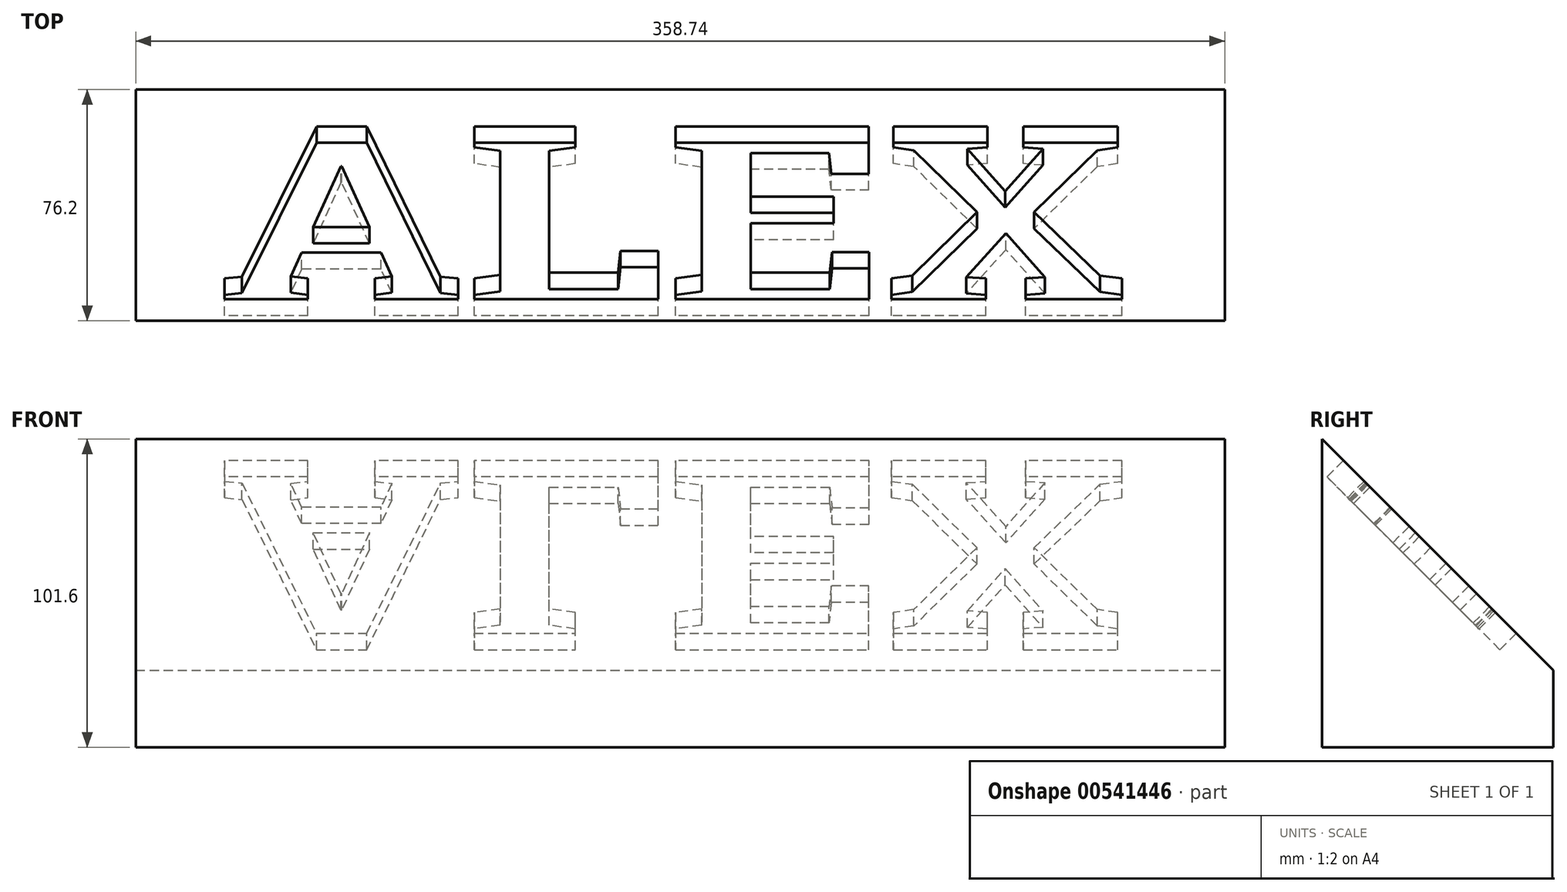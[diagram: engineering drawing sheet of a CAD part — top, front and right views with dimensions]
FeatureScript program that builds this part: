
annotation { "Feature Type Name" : "Feature", "Feature Type Description" : "" }
export const myFeature = defineFeature(function(context is Context, id is Id, definition is map)
    precondition{}
    {
        {
            var Q0;
            Q0=qCreatedBy(makeId("Top.planeOp"),FACE);
            var sketch = newSketch(context, id + "F0", { "sketchPlane" : qUnion([Q0])});
            skLineSegment(sketch, "E0.left", {"start": v(179.37, -152.4) * mm, "end": v(179.37, -76.2) * mm});
            skLineSegment(sketch, "E0.right", {"start": v(-179.37, -152.4) * mm, "end": v(-179.37, -76.2) * mm});
            skLineSegment(sketch, "E1", {"start": v(-179.37, -76.2) * mm, "end": v(179.37, -76.2) * mm});
            skLineSegment(sketch, "E2", {"start": v(-179.37, -152.4) * mm, "end": v(179.37, -152.4) * mm});
            skSolve(sketch);
        }
        {
            var Q0;
            {var subQ0=sQuery(id+"F0.wireOp",EDGE,"E0.left");Q0=makeQuery(id+"F0.imprint","IMPRINT",FACE,{"disambiguationData":[TD([[makeQuery(id+"F0.imprint","IMPRINT",EDGE,{"derivedFrom":subQ0}),1.0]])]});}
            var Q1;
            {var subQ0=sQuery(id+"F0.wireOp",EDGE,"f78de060-f92b-4e90-a891-c1896b122fa7.2");var subQ1=sQuery(id+"F0.wireOp",EDGE,"f78de060-f92b-4e90-a891-c1896b122fa7.1");var subQ2=makeQuery(id+"F0.imprint","INTERSECT",VERTEX,{"derivedFrom":[subQ1,subQ0]});Q1=makeQuery(id+"F0.imprint","IMPRINT",FACE,{"disambiguationData":[TD([[makeQuery(id+"F0.imprint","IMPRINT",EDGE,{"disambiguationData":[TD([[subQ2,1.0]])],"derivedFrom":subQ1}),-1.0]])]});}
            extrude(context, id + "F1", {"entities" : qUnion([Q0, Q1]), "depth" : 101.6 * mm, "offsetDistance" : 25.4 * mm});
        }
        {
            var Q0;
            Q0=makeQuery(id+"F1.opExtrude","CAP_EDGE",EDGE,{"disambiguationData":[OSD([sQuery(id+"F0.wireOp",EDGE,"E1")])],"isStart":false});
            chamfer(context, id + "F2", {"entities" : qUnion([Q0]), "width" : 76.2 * mm, "tangentPropagation" : true});
        }
        {
            var Q0;
            Q0=makeQuery(id+"F2.opChamfer","BLEND_FACE",FACE,{"disambiguationData":[OSD([sQuery(id+"F0.wireOp",EDGE,"E1")])]});
            cPlane(context, id + "F3", {"entities" : qUnion([Q0]), "cplaneType" : CPlaneType.OFFSET, "offset" : 0 * mm, "width" : 152.4 * mm, "height" : 152.4 * mm});
        }
        {
            var Q0;
            Q0=qCreatedBy(id+"F3.planeOp",FACE);
            var sketch = newSketch(context, id + "F4", { "sketchPlane" : qUnion([Q0])});
            skPoint(sketch, "E3", {"position": v(-228.37, 282) * mm});
            skPoint(sketch, "E4.start.orphan", {"position": v(0, -72.57) * mm});
            skPoint(sketch, "E5", {"position": v(0, 128.8) * mm});
            skPoint(sketch, "E6", {"position": v(148.44, 119.79) * mm});
            skPoint(sketch, "E7", {"position": v(423, -106.18) * mm});
            skText(sketch, "E8", { "text": "ALEX", "fontName": "RobotoSlab-Bold.ttf"});
            const initialGuessF4  = {"E8": [0.1524, 0.1696, -1, 0, 0.08159]};
            skSetInitialGuess(sketch, initialGuessF4);
            skSolve(sketch);
        }
        {
            var Q0;
            Q0=qSketchRegion(id+"F4",true);
            extrude(context, id + "F5", {"entities" : qUnion([Q0]), "operationType" : NewBodyOperationType.REMOVE, "oppositeDirection" : true, "depth" : 7.62 * mm, "offsetDistance" : 25.4 * mm});
        }
    });
